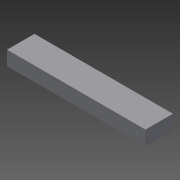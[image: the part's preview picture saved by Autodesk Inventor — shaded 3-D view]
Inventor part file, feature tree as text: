
AUTODESK INVENTOR PART (.ipt)
format: ipt  version: 2013 (Build 170138000, 138)  size: 65,536 bytes
history: native  units: in
note: dims shown in document units (in); Inventor stores cm internally (conversion verified against a paired STEP export)
features: extrude x1, sketch x1
ambient origin geometry x8: Origin, YZ Plane, XZ Plane, XY Plane, X Axis, Y Axis, Z Axis, Center Point
bodies: Solid1 (feature_tree)
feature tree (2):
  extrude  "Extrusion1"  Depth=10.5in
  sketch  "Sketch1"  dims[d0=53.0in d1=10.5in d2=5.5in d3=0.0in]
